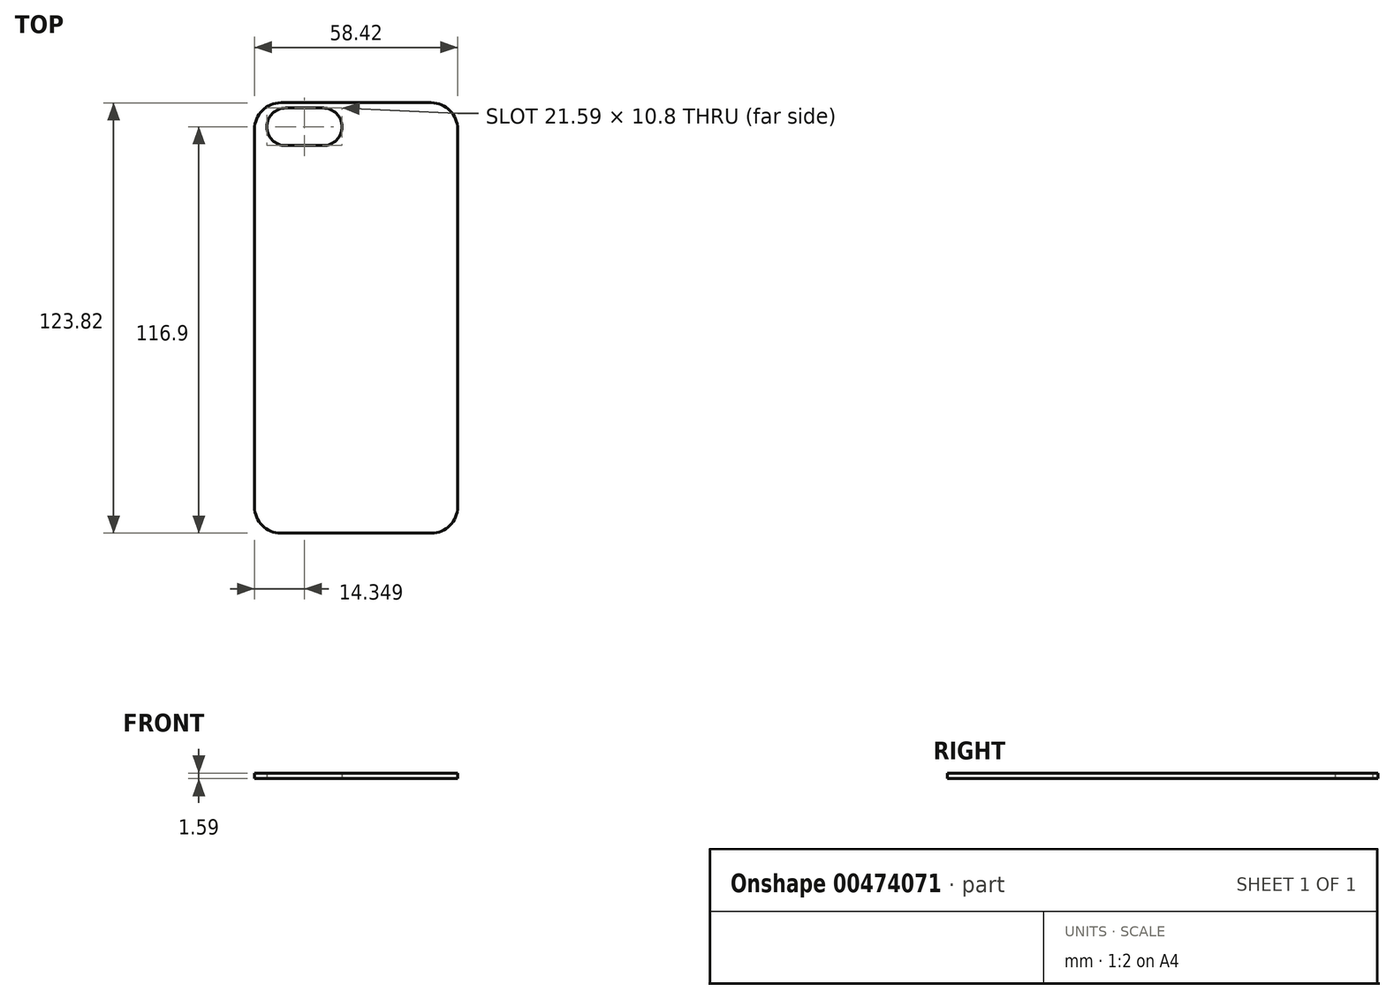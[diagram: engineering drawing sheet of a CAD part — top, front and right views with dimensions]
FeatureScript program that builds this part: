
annotation { "Feature Type Name" : "Feature", "Feature Type Description" : "" }
export const myFeature = defineFeature(function(context is Context, id is Id, definition is map)
    precondition{}
    {
        {
            var Q0;
            Q0=qCreatedBy(makeId("Top.planeOp"),FACE);
            var sketch = newSketch(context, id + "F0", { "sketchPlane" : qUnion([Q0])});
            skLineSegment(sketch, "E0.bottom", {"start": v(10.92, 125.3) * mm, "end": v(54.1, 125.3) * mm});
            skLineSegment(sketch, "E0.top", {"start": v(10.92, 1.48) * mm, "end": v(54.1, 1.48) * mm});
            skLineSegment(sketch, "E0.left", {"start": v(3.3, 117.68) * mm, "end": v(3.3, 9.1) * mm});
            skLineSegment(sketch, "E0.right", {"start": v(61.72, 117.68) * mm, "end": v(61.72, 9.1) * mm});
            skPoint(sketch, "E1.visualSharp", {"position": v(3.3, 125.3) * mm});
            skArc(sketch, "E1.filletArc", {"start": v(10.92, 125.3) * mm, "mid": v(5.53, 123.07) * mm, "end": v(3.3, 117.68) * mm});
            skPoint(sketch, "E2.visualSharp", {"position": v(61.72, 125.3) * mm});
            skArc(sketch, "E2.filletArc", {"start": v(61.72, 117.68) * mm, "mid": v(59.49, 123.07) * mm, "end": v(54.1, 125.3) * mm});
            skPoint(sketch, "E3.visualSharp", {"position": v(61.72, 1.48) * mm});
            skArc(sketch, "E3.filletArc", {"start": v(54.1, 1.48) * mm, "mid": v(59.49, 3.7) * mm, "end": v(61.72, 9.1) * mm});
            skPoint(sketch, "E4.visualSharp", {"position": v(3.3, 1.48) * mm});
            skArc(sketch, "E4.filletArc", {"start": v(3.3, 9.1) * mm, "mid": v(5.53, 3.7) * mm, "end": v(10.92, 1.48) * mm});
            skPoint(sketch, "E5.oppositeSnap0", {"position": v(5.53, 123.07) * mm});
            skLineSegment(sketch, "E5.bottom", {"start": v(23.05, 112.98) * mm, "end": v(12.25, 112.98) * mm});
            skLineSegment(sketch, "E5.top", {"start": v(23.05, 123.78) * mm, "end": v(12.25, 123.78) * mm});
            skLineSegment(sketch, "E5.left", {"start": v(28.44, 118.38) * mm, "end": v(28.44, 118.38) * mm});
            skLineSegment(sketch, "E5.right", {"start": v(6.85, 118.38) * mm, "end": v(6.85, 118.38) * mm});
            skPoint(sketch, "E6.visualSharp", {"position": v(6.85, 123.78) * mm});
            skArc(sketch, "E6.filletArc", {"start": v(12.25, 123.78) * mm, "mid": v(8.43, 122.2) * mm, "end": v(6.85, 118.38) * mm});
            skPoint(sketch, "E7.visualSharp", {"position": v(28.44, 123.78) * mm});
            skArc(sketch, "E7.filletArc", {"start": v(28.44, 118.38) * mm, "mid": v(26.86, 122.2) * mm, "end": v(23.05, 123.78) * mm});
            skPoint(sketch, "E8.visualSharp", {"position": v(6.85, 112.98) * mm});
            skArc(sketch, "E8.filletArc", {"start": v(6.85, 118.38) * mm, "mid": v(8.43, 114.56) * mm, "end": v(12.25, 112.98) * mm});
            skPoint(sketch, "E9.visualSharp", {"position": v(28.44, 112.98) * mm});
            skArc(sketch, "E9.filletArc", {"start": v(23.05, 112.98) * mm, "mid": v(26.86, 114.56) * mm, "end": v(28.44, 118.38) * mm});
            skSolve(sketch);
        }
        {
            var Q0;
            Q0=makeQuery(id+"F0.imprint","IMPRINT",FACE,{"disambiguationData":[TD([[makeQuery(id+"F0.imprint","IMPRINT",EDGE,{"derivedFrom":sQuery(id+"F0.wireOp",EDGE,"E0.bottom")}),-1.0]])]});
            extrude(context, id + "F1", {"entities" : qUnion([Q0]), "depth" : 1.59 * mm, "offsetDistance" : 25.4 * mm});
        }
    });
